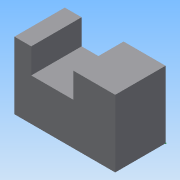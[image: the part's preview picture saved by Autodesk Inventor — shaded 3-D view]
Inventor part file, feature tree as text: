
AUTODESK INVENTOR PART (.ipt)
format: ipt  version: 2015 (Build 190159000, 159)  size: 76,800 bytes
history: native  units: in
note: dims shown in document units (in); Inventor stores cm internally (conversion verified against a paired STEP export)
features: sketch x2, extrude x1
ambient origin geometry x8: Origin, YZ Plane, XZ Plane, XY Plane, X Axis, Y Axis, Z Axis, Center Point
bodies: Solid1 (feature_tree)
feature tree (3):
  extrude  "Extrusion1"  Depth=0.3937in
  sketch  "Sketch2"  dims[d2=0.5906in d3=0.9843in d4=0.9843in d5=1.1811in d6=0.0in]
  sketch  "Sketch1"  dims[d0=1.5748in d1=0.3937in]
